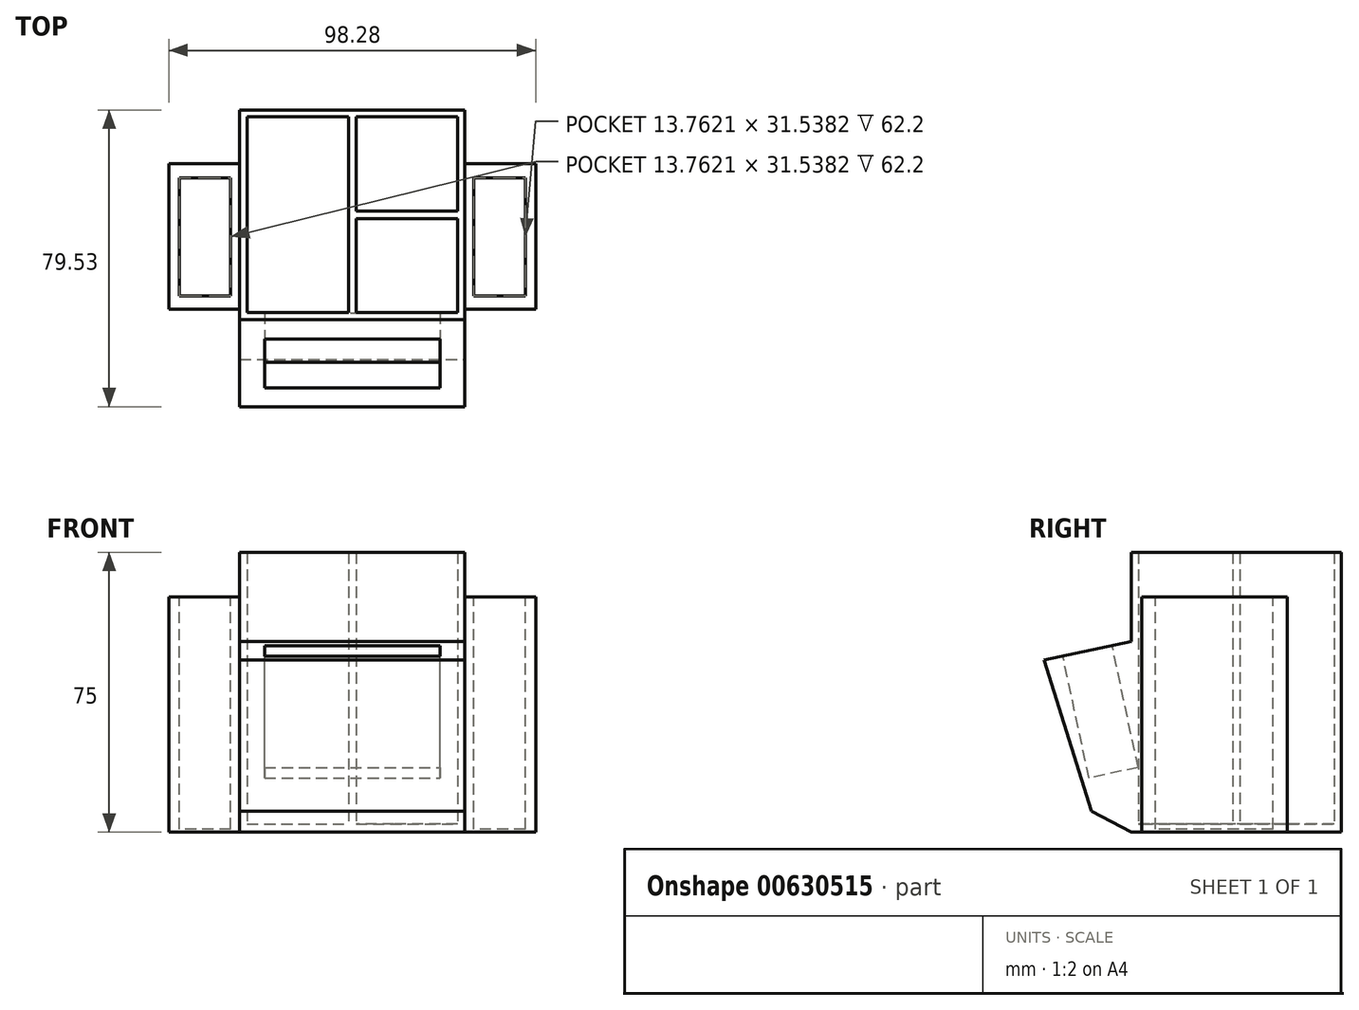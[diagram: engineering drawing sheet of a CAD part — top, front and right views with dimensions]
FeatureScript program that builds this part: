
annotation { "Feature Type Name" : "Feature", "Feature Type Description" : "" }
export const myFeature = defineFeature(function(context is Context, id is Id, definition is map)
    precondition{}
    {
        {
            var Q0;
            Q0=qCreatedBy(makeId("Top.planeOp"),FACE);
            var sketch = newSketch(context, id + "F0", { "sketchPlane" : qUnion([Q0])});
            skLineSegment(sketch, "E0.bottom", {"start": v(-30.14, 28.09) * mm, "end": v(30.14, 28.09) * mm});
            skLineSegment(sketch, "E0.top", {"start": v(-30.14, -28.09) * mm, "end": v(30.14, -28.09) * mm});
            skLineSegment(sketch, "E0.left", {"start": v(-30.14, 28.09) * mm, "end": v(-30.14, -28.09) * mm});
            skLineSegment(sketch, "E0.right", {"start": v(30.14, 28.09) * mm, "end": v(30.14, -28.09) * mm});
            skPoint(sketch, "E0.middle", {"position": v(0, 0) * mm});
            skLineSegment(sketch, "E1", {"start": v(0, 26.2) * mm, "end": v(0, 1) * mm});
            skLineSegment(sketch, "E2", {"start": v(0, 0) * mm, "end": v(28.2, 0) * mm});
            skLineSegment(sketch, "E3", {"start": v(30.14, 0) * mm, "end": v(30.14, 1) * mm});
            skLineSegment(sketch, "E4", {"start": v(30.14, 0) * mm, "end": v(30.14, -1) * mm});
            skLineSegment(sketch, "E5", {"start": v(28.2, -1) * mm, "end": v(1, -1) * mm});
            skLineSegment(sketch, "E6", {"start": v(28.2, 1) * mm, "end": v(1, 1) * mm});
            skLineSegment(sketch, "E7", {"start": v(0, 28.09) * mm, "end": v(1, 28.09) * mm});
            skLineSegment(sketch, "E8", {"start": v(1, 26.2) * mm, "end": v(1, 1) * mm});
            skLineSegment(sketch, "E9", {"start": v(0, 28.09) * mm, "end": v(-1, 28.09) * mm});
            skLineSegment(sketch, "E10", {"start": v(-1, 26.2) * mm, "end": v(-1, -26.2) * mm});
            skLineSegment(sketch, "E11", {"start": v(-1, -28.09) * mm, "end": v(1, -28.09) * mm});
            skPoint(sketch, "E12.orphan", {"position": v(0, 1) * mm});
            skLineSegment(sketch, "E13.trimOffspring", {"start": v(0, -1) * mm, "end": v(0, -26.2) * mm});
            skLineSegment(sketch, "E14", {"start": v(0, 1) * mm, "end": v(0, -1) * mm});
            skLineSegment(sketch, "E15.trimOffspring", {"start": v(1, -1) * mm, "end": v(1, -26.2) * mm});
            skLineSegment(sketch, "E16.bottom", {"start": v(-28.2, 26.2) * mm, "end": v(28.2, 26.2) * mm});
            skLineSegment(sketch, "E16.top", {"start": v(-28.2, -26.2) * mm, "end": v(28.2, -26.2) * mm});
            skLineSegment(sketch, "E16.left", {"start": v(-28.2, 26.2) * mm, "end": v(-28.2, -26.2) * mm});
            skLineSegment(sketch, "E16.right", {"start": v(28.2, 26.2) * mm, "end": v(28.2, -26.2) * mm});
            skPoint(sketch, "E17.orphan", {"position": v(0, -28.09) * mm});
            skSolve(sketch);
        }
        {
            var Q0;
            Q0 = qSketchRegion(id + "F0", true);
            var Q1;
            {var subQ3=sQuery(id+"F0.wireOp",EDGE,"E1");Q1=makeQuery(id+"F0.imprint","IMPRINT",FACE,{"disambiguationData":[TD([[makeQuery(id+"F0.imprint","IMPRINT",EDGE,{"derivedFrom":subQ3}),1.0]])]});}
            var Q2;
            {var subQ1=sQuery(id+"F0.wireOp",EDGE,"E2");Q2=makeQuery(id+"F0.imprint","IMPRINT",FACE,{"disambiguationData":[TD([[makeQuery(id+"F0.imprint","IMPRINT",EDGE,{"derivedFrom":subQ1}),-1.0]])]});}
            var Q3;
            {var subQ1=sQuery(id+"F0.wireOp",EDGE,"E1");Q3=makeQuery(id+"F0.imprint","IMPRINT",FACE,{"disambiguationData":[TD([[makeQuery(id+"F0.imprint","IMPRINT",EDGE,{"derivedFrom":subQ1}),-1.0]])]});}
            extrude(context, id + "F1", {"entities" : qUnion([Q0, Q1, Q2, Q3]), "depth" : 75 * mm, "offsetDistance" : 25 * mm});
        }
        {
            var Q0;
            Q0=qCreatedBy(makeId("Top.planeOp"),FACE);
            var sketch = newSketch(context, id + "F2", { "sketchPlane" : qUnion([Q0])});
            skLineSegment(sketch, "E18.bottom", {"start": v(-18.4, 26.23) * mm, "end": v(18.4, 26.23) * mm});
            skLineSegment(sketch, "E18.top", {"start": v(-18.4, -26.23) * mm, "end": v(18.4, -26.23) * mm});
            skPoint(sketch, "E18.middle", {"position": v(0, 0) * mm});
            skLineSegment(sketch, "E19.bottom", {"start": v(-28.2, 26.23) * mm, "end": v(28.2, 26.23) * mm});
            skLineSegment(sketch, "E19.top", {"start": v(-28.2, -26.23) * mm, "end": v(28.2, -26.23) * mm});
            skLineSegment(sketch, "E19.left", {"start": v(-28.2, 26.23) * mm, "end": v(-28.2, -26.23) * mm});
            skLineSegment(sketch, "E19.right", {"start": v(28.2, 26.23) * mm, "end": v(28.2, -26.23) * mm});
            skSolve(sketch);
        }
        {
            var Q0;
            {var subQ0=sQuery(id+"F2.wireOp",EDGE,"E19.left");Q0=makeQuery(id+"F2.imprint","IMPRINT",FACE,{"disambiguationData":[TD([[makeQuery(id+"F2.imprint","IMPRINT",EDGE,{"derivedFrom":subQ0}),1.0]])]});}
            extrude(context, id + "F3", {"entities" : qUnion([Q0]), "operationType" : NewBodyOperationType.ADD, "depth" : 2.2 * mm, "offsetDistance" : 25 * mm});
        }
        {
            var Q0;
            Q0=qCreatedBy(makeId("Right.planeOp"),FACE);
            var sketch = newSketch(context, id + "F4", { "sketchPlane" : qUnion([Q0])});
            skLineSegment(sketch, "E20.0.0", {"start": v(28.09, 0) * mm, "end": v(-28.09, 0) * mm});
            skLineSegment(sketch, "E20.0.1", {"start": v(-28.09, 0) * mm, "end": v(-28.09, 75) * mm});
            skLineSegment(sketch, "E20.0.2", {"start": v(-28.09, 75) * mm, "end": v(28.09, 75) * mm});
            skLineSegment(sketch, "E20.0.3", {"start": v(28.09, 75) * mm, "end": v(28.09, 0) * mm});
            skPoint(sketch, "E21.endSnap0", {"position": v(-28.09, 37.5) * mm});
            skLineSegment(sketch, "E22", {"start": v(-28.09, 0) * mm, "end": v(-38.76, 5.6) * mm});
            skLineSegment(sketch, "E23", {"start": v(-38.76, 5.6) * mm, "end": v(-51.44, 46.15) * mm});
            skLineSegment(sketch, "E24", {"start": v(-51.44, 46.15) * mm, "end": v(-28.09, 51.14) * mm});
            skSolve(sketch);
        }
        {
            var Q0;
            {var subQ0=sQuery(id+"F4.wireOp",EDGE,"uTZ441md-mFYq-b8y3-qvrN-TrnctnHwUMGK");Q0=makeQuery(id+"F4.imprint","IMPRINT",FACE,{"disambiguationData":[TD([[makeQuery(id+"F4.imprint","IMPRINT",EDGE,{"derivedFrom":subQ0}),-1.0]])]});}
            var Q1;
            {var subQ0=sQuery(id+"F4.wireOp",EDGE,"E22");Q1=makeQuery(id+"F4.imprint","IMPRINT",FACE,{"disambiguationData":[TD([[makeQuery(id+"F4.imprint","IMPRINT",EDGE,{"derivedFrom":subQ0}),-1.0]])]});}
            extrude(context, id + "F5", {"entities" : qUnion([Q0, Q1]), "operationType" : NewBodyOperationType.ADD, "oppositeDirection" : true, "depth" : 30.14 * mm, "offsetDistance" : 25 * mm, "hasSecondDirection" : true, "secondDirectionOppositeDirection" : false, "secondDirectionDepth" : 30.14 * mm});
        }
        {
            var Q0;
            Q0=makeQuery(id+"F5.opExtrude","SWEPT_FACE",FACE,{"disambiguationData":[OSD([sQuery(id+"F4.wireOp",EDGE,"E24")])]});
            var sketch = newSketch(context, id + "F6", { "sketchPlane" : qUnion([Q0])});
            skLineSegment(sketch, "E25.bottom", {"start": v(-23.5, -22.08) * mm, "end": v(23.5, -22.08) * mm});
            skLineSegment(sketch, "E25.top", {"start": v(-23.5, -35.56) * mm, "end": v(23.5, -35.56) * mm});
            skLineSegment(sketch, "E25.left", {"start": v(-23.5, -22.08) * mm, "end": v(-23.5, -35.56) * mm});
            skLineSegment(sketch, "E25.right", {"start": v(23.5, -22.08) * mm, "end": v(23.5, -35.56) * mm});
            skPoint(sketch, "E25.middle", {"position": v(0, -28.82) * mm});
            skSolve(sketch);
        }
        {
            var Q0;
            Q0 = qSketchRegion(id + "F6", true);
            extrude(context, id + "F7", {"entities" : qUnion([Q0]), "operationType" : NewBodyOperationType.REMOVE, "oppositeDirection" : true, "depth" : 33.4 * mm, "offsetDistance" : 25 * mm});
        }
        {
            var Q0;
            Q0=makeQuery(id+"F1.opExtrude","SWEPT_FACE",FACE,{"disambiguationData":[OSD([sQuery(id+"F0.wireOp",EDGE,"E0.left")])]});
            var sketch = newSketch(context, id + "F8", { "sketchPlane" : qUnion([Q0])});
            skLineSegment(sketch, "E26.bottom", {"start": v(-13.67, 0) * mm, "end": v(25.36, 0) * mm});
            skLineSegment(sketch, "E26.top", {"start": v(-13.67, 63.04) * mm, "end": v(25.36, 63.04) * mm});
            skLineSegment(sketch, "E26.left", {"start": v(-13.67, 0) * mm, "end": v(-13.67, 63.04) * mm});
            skLineSegment(sketch, "E26.right", {"start": v(25.36, 0) * mm, "end": v(25.36, 63.04) * mm});
            skSolve(sketch);
        }
        {
            var Q0;
            Q0=makeQuery(id+"F1.opExtrude","SWEPT_FACE",FACE,{"disambiguationData":[OSD([sQuery(id+"F0.wireOp",EDGE,"E0.right"),sQuery(id+"F0.wireOp",EDGE,"E3"),sQuery(id+"F0.wireOp",EDGE,"E4")])]});
            var sketch = newSketch(context, id + "F9", { "sketchPlane" : qUnion([Q0])});
            skLineSegment(sketch, "E27.0", {"start": v(13.67, 63.04) * mm, "end": v(-25.36, 63.04) * mm});
            skLineSegment(sketch, "E28.0", {"start": v(13.67, 0) * mm, "end": v(13.67, 63.04) * mm});
            skLineSegment(sketch, "E29.0", {"start": v(13.67, 0) * mm, "end": v(-25.36, 0) * mm});
            skLineSegment(sketch, "E30.0", {"start": v(-25.36, 0) * mm, "end": v(-25.36, 63.04) * mm});
            skSolve(sketch);
        }
        {
            var Q0;
            Q0=makeQuery(id+"F8.imprint","IMPRINT",FACE,{"disambiguationData":[TD([[makeQuery(id+"F8.imprint","IMPRINT",EDGE,{"derivedFrom":sQuery(id+"F8.wireOp",EDGE,"E26.bottom")}),1.0]])]});
            var Q1;
            Q1=makeQuery(id+"F9.imprint","IMPRINT",FACE,{"disambiguationData":[TD([[makeQuery(id+"F9.imprint","IMPRINT",EDGE,{"derivedFrom":sQuery(id+"F9.wireOp",EDGE,"E27.0")}),1.0]])]});
            extrude(context, id + "F10", {"entities" : qUnion([Q0, Q1]), "operationType" : NewBodyOperationType.ADD, "depth" : 19 * mm, "offsetDistance" : 25 * mm, "hasSecondDirection" : true, "secondDirectionOppositeDirection" : true, "secondDirectionDepth" : 19 * mm});
        }
        {
            var Q0;
            {var subQ2=sQuery(id+"F8.wireOp",EDGE,"E26.top");Q0=makeQuery(id+"F10.boolean.opBoolean","SPLIT",FACE,{"disambiguationData":[TD([makeQuery(id+"F1.opExtrude","SWEPT_FACE",FACE,{"disambiguationData":[OSD([sQuery(id+"F0.wireOp",EDGE,"E16.left")])]})])],"derivedFrom":makeQuery(id+"F10.opExtrude","SWEPT_FACE",FACE,{"disambiguationData":[OSD([subQ2])]})});}
            var Q1;
            {var subQ0=sQuery(id+"F0.wireOp",EDGE,"E5");var subQ3=sQuery(id+"F9.wireOp",EDGE,"E27.0");Q1=makeQuery(id+"F10.boolean.opBoolean","SPLIT",FACE,{"disambiguationData":[TD([makeQuery(id+"F1.opExtrude","SWEPT_FACE",FACE,{"disambiguationData":[OSD([subQ0])]})])],"derivedFrom":makeQuery(id+"F10.opExtrude","SWEPT_FACE",FACE,{"disambiguationData":[OSD([subQ3])]})});}
            var Q2;
            {var subQ0=sQuery(id+"F0.wireOp",EDGE,"E6");var subQ3=sQuery(id+"F9.wireOp",EDGE,"E27.0");Q2=makeQuery(id+"F10.boolean.opBoolean","SPLIT",FACE,{"disambiguationData":[TD([makeQuery(id+"F1.opExtrude","SWEPT_FACE",FACE,{"disambiguationData":[OSD([subQ0])]})])],"derivedFrom":makeQuery(id+"F10.opExtrude","SWEPT_FACE",FACE,{"disambiguationData":[OSD([subQ3])]})});}
            extrude(context, id + "F11", {"entities" : qUnion([Q0, Q1, Q2]), "operationType" : NewBodyOperationType.REMOVE, "oppositeDirection" : true, "depth" : 60.83 * mm, "offsetDistance" : 25 * mm});
        }
        {
            var Q0;
            {var subQ2=sQuery(id+"F9.wireOp",EDGE,"E27.0");Q0=makeQuery(id+"F10.boolean.opBoolean","SPLIT",FACE,{"disambiguationData":[TD([makeQuery(id+"F1.opExtrude","SWEPT_FACE",FACE,{"disambiguationData":[OSD([sQuery(id+"F0.wireOp",EDGE,"E0.right"),sQuery(id+"F0.wireOp",EDGE,"E3"),sQuery(id+"F0.wireOp",EDGE,"E4")])]})])],"derivedFrom":makeQuery(id+"F10.opExtrude","SWEPT_FACE",FACE,{"disambiguationData":[OSD([subQ2])]})});}
            var sketch = newSketch(context, id + "F12", { "sketchPlane" : qUnion([Q0])});
            skLineSegment(sketch, "E31", {"start": v(-38.7, 9.65) * mm, "end": v(-38.7, -21.7) * mm});
            skLineSegment(sketch, "E32", {"start": v(-38.7, -21.7) * mm, "end": v(-32.59, -21.7) * mm});
            skLineSegment(sketch, "E33", {"start": v(-32.59, -21.7) * mm, "end": v(-32.59, 9.84) * mm});
            skLineSegment(sketch, "E34", {"start": v(-32.59, 9.84) * mm, "end": v(-38.7, 9.84) * mm});
            skLineSegment(sketch, "E35", {"start": v(-38.7, 9.84) * mm, "end": v(-38.7, 9.65) * mm});
            skLineSegment(sketch, "E36.MirrorCS", {"start": v(32.59, 9.84) * mm, "end": v(38.7, 9.84) * mm});
            skLineSegment(sketch, "E37.MirrorCS", {"start": v(38.7, 9.65) * mm, "end": v(38.7, -21.7) * mm});
            skLineSegment(sketch, "E38.MirrorCS", {"start": v(32.59, -21.7) * mm, "end": v(32.59, 9.84) * mm});
            skLineSegment(sketch, "E39.MirrorCS", {"start": v(38.7, -21.7) * mm, "end": v(32.59, -21.7) * mm});
            skLineSegment(sketch, "E40.MirrorCS", {"start": v(38.7, 9.84) * mm, "end": v(38.7, 9.65) * mm});
            skLineSegment(sketch, "E41", {"start": v(-38.7, 9.84) * mm, "end": v(-46.35, 9.84) * mm});
            skLineSegment(sketch, "E42", {"start": v(-46.35, 9.84) * mm, "end": v(-46.35, -21.12) * mm});
            skLineSegment(sketch, "E43", {"start": v(-46.35, -21.12) * mm, "end": v(-46.35, -21.7) * mm});
            skLineSegment(sketch, "E44", {"start": v(-46.35, -21.7) * mm, "end": v(-38.7, -21.7) * mm});
            skLineSegment(sketch, "E45.MirrorCS", {"start": v(46.35, -21.7) * mm, "end": v(38.7, -21.7) * mm});
            skLineSegment(sketch, "E46.MirrorCS", {"start": v(46.35, -21.12) * mm, "end": v(46.35, -21.7) * mm});
            skLineSegment(sketch, "E47.MirrorCS", {"start": v(38.7, 9.84) * mm, "end": v(46.35, 9.84) * mm});
            skLineSegment(sketch, "E48.MirrorCS", {"start": v(46.35, 9.84) * mm, "end": v(46.35, -21.12) * mm});
            skSolve(sketch);
        }
        {
            var Q0;
            Q0 = qSketchRegion(id + "F12", true);
            extrude(context, id + "F13", {"entities" : qUnion([Q0]), "operationType" : NewBodyOperationType.REMOVE, "oppositeDirection" : true, "depth" : 62.2 * mm, "offsetDistance" : 25 * mm});
        }
    });
